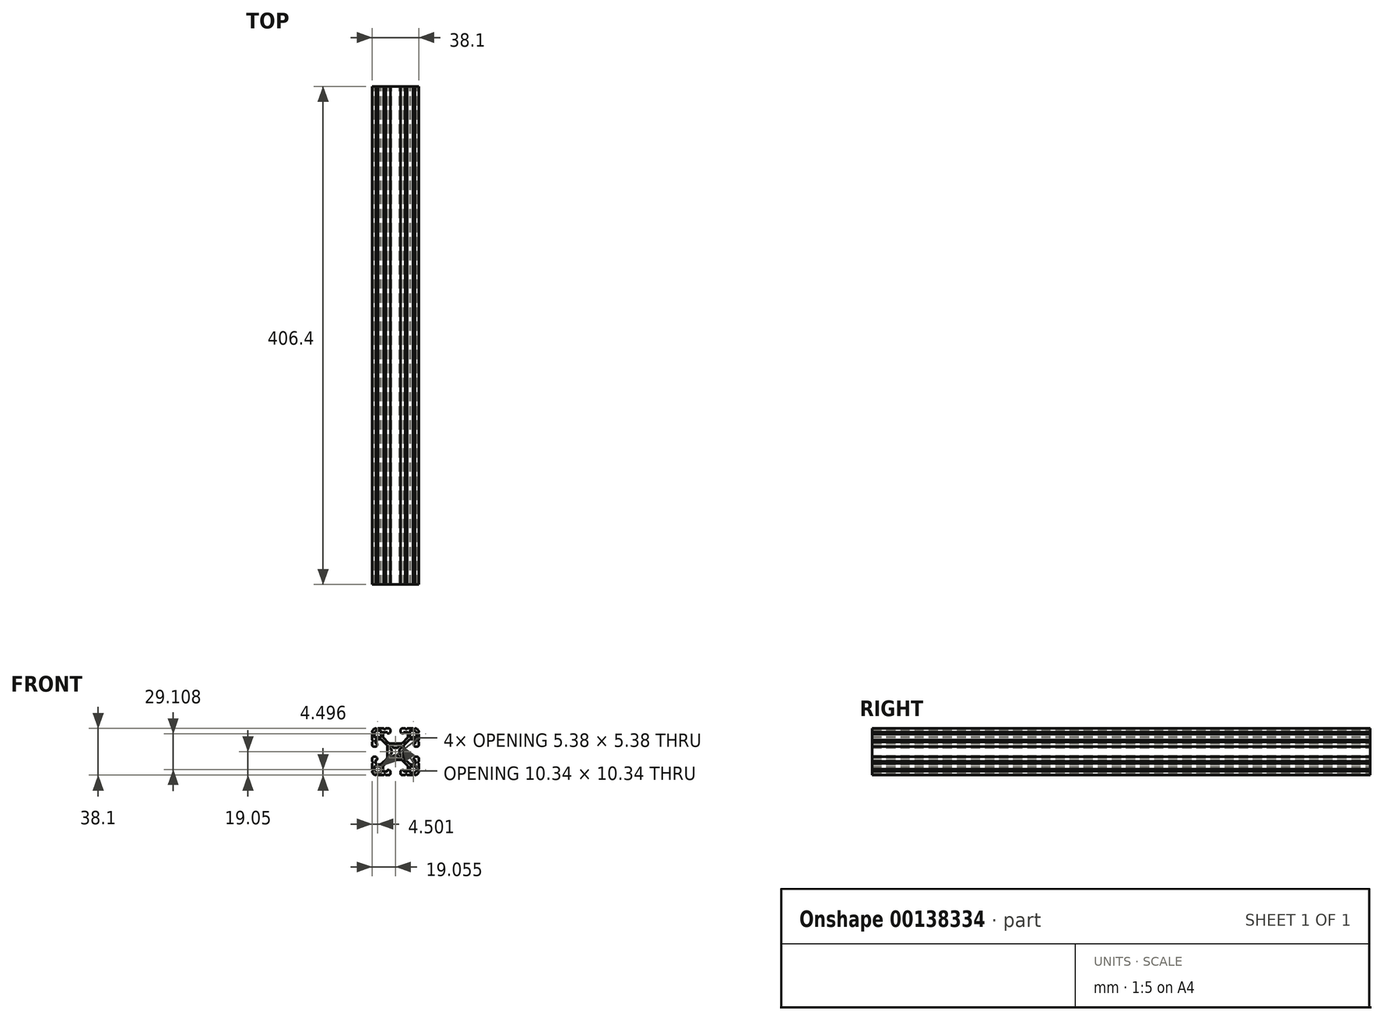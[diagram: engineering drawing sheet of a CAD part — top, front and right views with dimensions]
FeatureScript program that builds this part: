
annotation { "Feature Type Name" : "Feature", "Feature Type Description" : "" }
export const myFeature = defineFeature(function(context is Context, id is Id, definition is map)
    precondition{}
    {
        {
            var Q0;
            Q0=qCreatedBy(makeId("Front.planeOp"),FACE);
            var sketch = newSketch(context, id + "F0", { "sketchPlane" : qUnion([Q0])});
            skLineSegment(sketch, "E0", {"start": v(-126.4, 59.55) * mm, "end": v(-126.4, 54.72) * mm});
            skArc(sketch, "E1", {"start": v(-126.4, 53.2) * mm, "mid": v(-125.63, 53.96) * mm, "end": v(-126.4, 54.72) * mm});
            skArc(sketch, "E2", {"start": v(-126.4, 53.2) * mm, "mid": v(-125.47, 50.93) * mm, "end": v(-123.2, 50) * mm});
            skArc(sketch, "E3", {"start": v(-121.67, 50) * mm, "mid": v(-122.43, 50.76) * mm, "end": v(-123.2, 50) * mm});
            skLineSegment(sketch, "E4", {"start": v(-121.67, 50) * mm, "end": v(-116.84, 50) * mm});
            skArc(sketch, "E5", {"start": v(-115.32, 50) * mm, "mid": v(-116.08, 50.76) * mm, "end": v(-116.84, 50) * mm});
            skLineSegment(sketch, "E6", {"start": v(-115.32, 50) * mm, "end": v(-112.98, 50) * mm});
            skArc(sketch, "E7", {"start": v(-112.98, 50) * mm, "mid": v(-111.87, 50.46) * mm, "end": v(-111.4, 51.57) * mm});
            skLineSegment(sketch, "E8", {"start": v(-111.4, 51.57) * mm, "end": v(-111.4, 52.49) * mm});
            skArc(sketch, "E9", {"start": v(-111.4, 52.49) * mm, "mid": v(-111.87, 53.6) * mm, "end": v(-112.98, 54.06) * mm});
            skLineSegment(sketch, "E10", {"start": v(-112.98, 54.06) * mm, "end": v(-113.7, 54.06) * mm});
            skArc(sketch, "E11", {"start": v(-113.7, 54.06) * mm, "mid": v(-113.96, 53.95) * mm, "end": v(-114.08, 53.68) * mm});
            skLineSegment(sketch, "E12", {"start": v(-114.08, 53.68) * mm, "end": v(-114.08, 53.35) * mm});
            skArc(sketch, "E13", {"start": v(-114.46, 52.97) * mm, "mid": v(-114.19, 53.08) * mm, "end": v(-114.08, 53.35) * mm});
            skLineSegment(sketch, "E14", {"start": v(-114.46, 52.97) * mm, "end": v(-116.74, 52.97) * mm});
            skArc(sketch, "E15", {"start": v(-117.63, 53.86) * mm, "mid": v(-117.37, 53.23) * mm, "end": v(-116.74, 52.97) * mm});
            skLineSegment(sketch, "E16", {"start": v(-117.63, 53.86) * mm, "end": v(-117.63, 56.67) * mm});
            skArc(sketch, "E17", {"start": v(-117.26, 57.57) * mm, "mid": v(-117.54, 57.16) * mm, "end": v(-117.63, 56.67) * mm});
            skLineSegment(sketch, "E18", {"start": v(-117.26, 57.57) * mm, "end": v(-112.9, 61.93) * mm});
            skArc(sketch, "E19", {"start": v(-112, 62.3) * mm, "mid": v(-112.49, 62.2) * mm, "end": v(-112.9, 61.93) * mm});
            skLineSegment(sketch, "E20", {"start": v(-112, 62.3) * mm, "end": v(-102.7, 62.3) * mm});
            skArc(sketch, "E21", {"start": v(-101.8, 61.93) * mm, "mid": v(-102.2, 62.2) * mm, "end": v(-102.7, 62.3) * mm});
            skLineSegment(sketch, "E22", {"start": v(-101.8, 61.93) * mm, "end": v(-97.43, 57.57) * mm});
            skArc(sketch, "E23", {"start": v(-97.06, 56.67) * mm, "mid": v(-97.15, 57.16) * mm, "end": v(-97.43, 57.57) * mm});
            skLineSegment(sketch, "E24", {"start": v(-97.06, 56.67) * mm, "end": v(-97.06, 53.86) * mm});
            skArc(sketch, "E25", {"start": v(-97.95, 52.97) * mm, "mid": v(-97.32, 53.23) * mm, "end": v(-97.06, 53.86) * mm});
            skLineSegment(sketch, "E26", {"start": v(-97.95, 52.97) * mm, "end": v(-100.23, 52.97) * mm});
            skArc(sketch, "E27", {"start": v(-100.61, 53.35) * mm, "mid": v(-100.5, 53.08) * mm, "end": v(-100.23, 52.97) * mm});
            skLineSegment(sketch, "E28", {"start": v(-100.61, 53.35) * mm, "end": v(-100.61, 53.68) * mm});
            skArc(sketch, "E29", {"start": v(-100.61, 53.68) * mm, "mid": v(-100.73, 53.95) * mm, "end": v(-101, 54.06) * mm});
            skLineSegment(sketch, "E30", {"start": v(-101, 54.06) * mm, "end": v(-101.7, 54.06) * mm});
            skArc(sketch, "E31", {"start": v(-101.7, 54.06) * mm, "mid": v(-102.82, 53.6) * mm, "end": v(-103.28, 52.49) * mm});
            skLineSegment(sketch, "E32", {"start": v(-103.28, 52.49) * mm, "end": v(-103.28, 51.57) * mm});
            skArc(sketch, "E33", {"start": v(-103.28, 51.57) * mm, "mid": v(-102.82, 50.46) * mm, "end": v(-101.7, 50) * mm});
            skLineSegment(sketch, "E34", {"start": v(-101.7, 50) * mm, "end": v(-99.37, 50) * mm});
            skArc(sketch, "E35", {"start": v(-97.85, 50) * mm, "mid": v(-98.6, 50.76) * mm, "end": v(-99.37, 50) * mm});
            skLineSegment(sketch, "E36", {"start": v(-97.85, 50) * mm, "end": v(-93.02, 50) * mm});
            skArc(sketch, "E37", {"start": v(-91.5, 50) * mm, "mid": v(-92.26, 50.76) * mm, "end": v(-93.02, 50) * mm});
            skArc(sketch, "E38", {"start": v(-91.5, 50) * mm, "mid": v(-89.23, 50.93) * mm, "end": v(-88.3, 53.2) * mm});
            skArc(sketch, "E39", {"start": v(-88.3, 54.72) * mm, "mid": v(-89.06, 53.96) * mm, "end": v(-88.3, 53.2) * mm});
            skLineSegment(sketch, "E40", {"start": v(-88.3, 54.72) * mm, "end": v(-88.3, 59.55) * mm});
            skArc(sketch, "E41", {"start": v(-88.3, 61.07) * mm, "mid": v(-89.06, 60.31) * mm, "end": v(-88.3, 59.55) * mm});
            skLineSegment(sketch, "E42", {"start": v(-88.3, 61.07) * mm, "end": v(-88.3, 63.41) * mm});
            skArc(sketch, "E43", {"start": v(-88.3, 63.41) * mm, "mid": v(-88.76, 64.52) * mm, "end": v(-89.87, 64.99) * mm});
            skLineSegment(sketch, "E44", {"start": v(-89.87, 64.99) * mm, "end": v(-90.78, 64.99) * mm});
            skArc(sketch, "E45", {"start": v(-90.78, 64.99) * mm, "mid": v(-91.9, 64.52) * mm, "end": v(-92.36, 63.41) * mm});
            skLineSegment(sketch, "E46", {"start": v(-92.36, 63.41) * mm, "end": v(-92.36, 62.7) * mm});
            skArc(sketch, "E47", {"start": v(-92.36, 62.7) * mm, "mid": v(-92.25, 62.43) * mm, "end": v(-91.98, 62.32) * mm});
            skLineSegment(sketch, "E48", {"start": v(-91.98, 62.32) * mm, "end": v(-91.65, 62.32) * mm});
            skArc(sketch, "E49", {"start": v(-91.27, 61.94) * mm, "mid": v(-91.38, 62.2) * mm, "end": v(-91.65, 62.32) * mm});
            skLineSegment(sketch, "E50", {"start": v(-91.27, 61.94) * mm, "end": v(-91.27, 59.65) * mm});
            skArc(sketch, "E51", {"start": v(-92.16, 58.76) * mm, "mid": v(-91.53, 59.02) * mm, "end": v(-91.27, 59.65) * mm});
            skLineSegment(sketch, "E52", {"start": v(-92.16, 58.76) * mm, "end": v(-94.97, 58.76) * mm});
            skArc(sketch, "E53", {"start": v(-95.87, 59.13) * mm, "mid": v(-95.46, 58.86) * mm, "end": v(-94.97, 58.76) * mm});
            skLineSegment(sketch, "E54", {"start": v(-95.87, 59.13) * mm, "end": v(-100.23, 63.5) * mm});
            skArc(sketch, "E55", {"start": v(-100.6, 64.4) * mm, "mid": v(-100.5, 63.9) * mm, "end": v(-100.23, 63.5) * mm});
            skLineSegment(sketch, "E56", {"start": v(-100.6, 64.4) * mm, "end": v(-100.6, 73.7) * mm});
            skArc(sketch, "E57", {"start": v(-100.23, 74.6) * mm, "mid": v(-100.5, 74.2) * mm, "end": v(-100.6, 73.7) * mm});
            skLineSegment(sketch, "E58", {"start": v(-100.23, 74.6) * mm, "end": v(-95.87, 78.96) * mm});
            skArc(sketch, "E59", {"start": v(-94.97, 79.34) * mm, "mid": v(-95.46, 79.24) * mm, "end": v(-95.87, 78.96) * mm});
            skLineSegment(sketch, "E60", {"start": v(-94.97, 79.34) * mm, "end": v(-92.16, 79.34) * mm});
            skArc(sketch, "E61", {"start": v(-91.27, 78.45) * mm, "mid": v(-91.53, 79.08) * mm, "end": v(-92.16, 79.34) * mm});
            skLineSegment(sketch, "E62", {"start": v(-91.27, 78.45) * mm, "end": v(-91.27, 76.16) * mm});
            skArc(sketch, "E63", {"start": v(-91.65, 75.78) * mm, "mid": v(-91.38, 75.9) * mm, "end": v(-91.27, 76.16) * mm});
            skLineSegment(sketch, "E64", {"start": v(-91.65, 75.78) * mm, "end": v(-91.98, 75.78) * mm});
            skArc(sketch, "E65", {"start": v(-91.98, 75.78) * mm, "mid": v(-92.25, 75.67) * mm, "end": v(-92.36, 75.4) * mm});
            skLineSegment(sketch, "E66", {"start": v(-92.36, 75.4) * mm, "end": v(-92.36, 74.69) * mm});
            skArc(sketch, "E67", {"start": v(-92.36, 74.69) * mm, "mid": v(-91.9, 73.58) * mm, "end": v(-90.78, 73.11) * mm});
            skLineSegment(sketch, "E68", {"start": v(-90.78, 73.11) * mm, "end": v(-89.87, 73.11) * mm});
            skArc(sketch, "E69", {"start": v(-89.87, 73.11) * mm, "mid": v(-88.76, 73.58) * mm, "end": v(-88.3, 74.69) * mm});
            skLineSegment(sketch, "E70", {"start": v(-88.3, 74.69) * mm, "end": v(-88.3, 77.03) * mm});
            skArc(sketch, "E71", {"start": v(-88.3, 78.55) * mm, "mid": v(-89.06, 77.79) * mm, "end": v(-88.3, 77.03) * mm});
            skLineSegment(sketch, "E72", {"start": v(-88.3, 78.55) * mm, "end": v(-88.3, 83.38) * mm});
            skArc(sketch, "E73", {"start": v(-88.3, 84.9) * mm, "mid": v(-89.06, 84.14) * mm, "end": v(-88.3, 83.38) * mm});
            skArc(sketch, "E74", {"start": v(-88.3, 84.9) * mm, "mid": v(-89.23, 87.17) * mm, "end": v(-91.5, 88.1) * mm});
            skArc(sketch, "E75", {"start": v(-93.02, 88.1) * mm, "mid": v(-92.26, 87.34) * mm, "end": v(-91.5, 88.1) * mm});
            skLineSegment(sketch, "E76", {"start": v(-93.02, 88.1) * mm, "end": v(-97.85, 88.1) * mm});
            skArc(sketch, "E77", {"start": v(-99.37, 88.1) * mm, "mid": v(-98.6, 87.34) * mm, "end": v(-97.85, 88.1) * mm});
            skLineSegment(sketch, "E78", {"start": v(-99.37, 88.1) * mm, "end": v(-101.7, 88.1) * mm});
            skArc(sketch, "E79", {"start": v(-101.7, 88.1) * mm, "mid": v(-102.82, 87.64) * mm, "end": v(-103.28, 86.53) * mm});
            skLineSegment(sketch, "E80", {"start": v(-103.28, 86.53) * mm, "end": v(-103.28, 85.61) * mm});
            skArc(sketch, "E81", {"start": v(-103.28, 85.61) * mm, "mid": v(-102.82, 84.5) * mm, "end": v(-101.7, 84.04) * mm});
            skLineSegment(sketch, "E82", {"start": v(-101.7, 84.04) * mm, "end": v(-101, 84.04) * mm});
            skArc(sketch, "E83", {"start": v(-101, 84.04) * mm, "mid": v(-100.73, 84.15) * mm, "end": v(-100.61, 84.42) * mm});
            skLineSegment(sketch, "E84", {"start": v(-100.61, 84.42) * mm, "end": v(-100.61, 84.75) * mm});
            skArc(sketch, "E85", {"start": v(-100.23, 85.13) * mm, "mid": v(-100.5, 85.02) * mm, "end": v(-100.61, 84.75) * mm});
            skLineSegment(sketch, "E86", {"start": v(-100.23, 85.13) * mm, "end": v(-97.95, 85.13) * mm});
            skArc(sketch, "E87", {"start": v(-97.06, 84.24) * mm, "mid": v(-97.32, 84.87) * mm, "end": v(-97.95, 85.13) * mm});
            skLineSegment(sketch, "E88", {"start": v(-97.06, 84.24) * mm, "end": v(-97.06, 81.43) * mm});
            skArc(sketch, "E89", {"start": v(-97.43, 80.53) * mm, "mid": v(-97.15, 80.94) * mm, "end": v(-97.06, 81.43) * mm});
            skLineSegment(sketch, "E90", {"start": v(-97.43, 80.53) * mm, "end": v(-101.8, 76.17) * mm});
            skArc(sketch, "E91", {"start": v(-102.7, 75.8) * mm, "mid": v(-102.2, 75.9) * mm, "end": v(-101.8, 76.17) * mm});
            skLineSegment(sketch, "E92", {"start": v(-102.7, 75.8) * mm, "end": v(-112, 75.8) * mm});
            skArc(sketch, "E93", {"start": v(-112.9, 76.17) * mm, "mid": v(-112.49, 75.9) * mm, "end": v(-112, 75.8) * mm});
            skLineSegment(sketch, "E94", {"start": v(-112.9, 76.17) * mm, "end": v(-117.26, 80.53) * mm});
            skArc(sketch, "E95", {"start": v(-117.63, 81.43) * mm, "mid": v(-117.54, 80.94) * mm, "end": v(-117.26, 80.53) * mm});
            skLineSegment(sketch, "E96", {"start": v(-117.63, 81.43) * mm, "end": v(-117.63, 84.24) * mm});
            skArc(sketch, "E97", {"start": v(-116.74, 85.13) * mm, "mid": v(-117.37, 84.87) * mm, "end": v(-117.63, 84.24) * mm});
            skLineSegment(sketch, "E98", {"start": v(-116.74, 85.13) * mm, "end": v(-114.46, 85.13) * mm});
            skArc(sketch, "E99", {"start": v(-114.08, 84.75) * mm, "mid": v(-114.19, 85.02) * mm, "end": v(-114.46, 85.13) * mm});
            skLineSegment(sketch, "E100", {"start": v(-114.08, 84.75) * mm, "end": v(-114.08, 84.42) * mm});
            skArc(sketch, "E101", {"start": v(-114.08, 84.42) * mm, "mid": v(-113.96, 84.15) * mm, "end": v(-113.7, 84.04) * mm});
            skLineSegment(sketch, "E102", {"start": v(-113.7, 84.04) * mm, "end": v(-112.98, 84.04) * mm});
            skArc(sketch, "E103", {"start": v(-112.98, 84.04) * mm, "mid": v(-111.87, 84.5) * mm, "end": v(-111.4, 85.61) * mm});
            skLineSegment(sketch, "E104", {"start": v(-111.4, 85.61) * mm, "end": v(-111.4, 86.53) * mm});
            skArc(sketch, "E105", {"start": v(-111.4, 86.53) * mm, "mid": v(-111.87, 87.64) * mm, "end": v(-112.98, 88.1) * mm});
            skLineSegment(sketch, "E106", {"start": v(-112.98, 88.1) * mm, "end": v(-115.32, 88.1) * mm});
            skArc(sketch, "E107", {"start": v(-116.84, 88.1) * mm, "mid": v(-116.08, 87.34) * mm, "end": v(-115.32, 88.1) * mm});
            skLineSegment(sketch, "E108", {"start": v(-116.84, 88.1) * mm, "end": v(-121.67, 88.1) * mm});
            skArc(sketch, "E109", {"start": v(-123.2, 88.1) * mm, "mid": v(-122.43, 87.34) * mm, "end": v(-121.67, 88.1) * mm});
            skArc(sketch, "E110", {"start": v(-123.2, 88.1) * mm, "mid": v(-125.47, 87.17) * mm, "end": v(-126.4, 84.9) * mm});
            skArc(sketch, "E111", {"start": v(-126.4, 83.38) * mm, "mid": v(-125.63, 84.14) * mm, "end": v(-126.4, 84.9) * mm});
            skLineSegment(sketch, "E112", {"start": v(-126.4, 83.38) * mm, "end": v(-126.4, 78.55) * mm});
            skArc(sketch, "E113", {"start": v(-126.4, 77.03) * mm, "mid": v(-125.63, 77.79) * mm, "end": v(-126.4, 78.55) * mm});
            skLineSegment(sketch, "E114", {"start": v(-126.4, 77.03) * mm, "end": v(-126.4, 74.69) * mm});
            skArc(sketch, "E115", {"start": v(-126.4, 74.69) * mm, "mid": v(-125.93, 73.58) * mm, "end": v(-124.82, 73.11) * mm});
            skLineSegment(sketch, "E116", {"start": v(-124.82, 73.11) * mm, "end": v(-123.9, 73.11) * mm});
            skArc(sketch, "E117", {"start": v(-123.9, 73.11) * mm, "mid": v(-122.8, 73.58) * mm, "end": v(-122.33, 74.69) * mm});
            skLineSegment(sketch, "E118", {"start": v(-122.33, 74.69) * mm, "end": v(-122.33, 75.4) * mm});
            skArc(sketch, "E119", {"start": v(-122.33, 75.4) * mm, "mid": v(-122.44, 75.67) * mm, "end": v(-122.71, 75.78) * mm});
            skLineSegment(sketch, "E120", {"start": v(-122.71, 75.78) * mm, "end": v(-123.04, 75.78) * mm});
            skArc(sketch, "E121", {"start": v(-123.42, 76.16) * mm, "mid": v(-123.31, 75.9) * mm, "end": v(-123.04, 75.78) * mm});
            skLineSegment(sketch, "E122", {"start": v(-123.42, 76.16) * mm, "end": v(-123.42, 78.45) * mm});
            skArc(sketch, "E123", {"start": v(-122.53, 79.34) * mm, "mid": v(-123.16, 79.08) * mm, "end": v(-123.42, 78.45) * mm});
            skLineSegment(sketch, "E124", {"start": v(-122.53, 79.34) * mm, "end": v(-119.72, 79.34) * mm});
            skArc(sketch, "E125", {"start": v(-118.82, 78.96) * mm, "mid": v(-119.23, 79.24) * mm, "end": v(-119.72, 79.34) * mm});
            skLineSegment(sketch, "E126", {"start": v(-118.82, 78.96) * mm, "end": v(-114.46, 74.6) * mm});
            skArc(sketch, "E127", {"start": v(-114.09, 73.7) * mm, "mid": v(-114.19, 74.2) * mm, "end": v(-114.46, 74.6) * mm});
            skLineSegment(sketch, "E128", {"start": v(-114.09, 73.7) * mm, "end": v(-114.09, 64.4) * mm});
            skArc(sketch, "E129", {"start": v(-114.46, 63.5) * mm, "mid": v(-114.19, 63.9) * mm, "end": v(-114.09, 64.4) * mm});
            skLineSegment(sketch, "E130", {"start": v(-114.46, 63.5) * mm, "end": v(-118.82, 59.13) * mm});
            skArc(sketch, "E131", {"start": v(-119.72, 58.76) * mm, "mid": v(-119.23, 58.86) * mm, "end": v(-118.82, 59.13) * mm});
            skLineSegment(sketch, "E132", {"start": v(-119.72, 58.76) * mm, "end": v(-122.53, 58.76) * mm});
            skArc(sketch, "E133", {"start": v(-123.42, 59.65) * mm, "mid": v(-123.16, 59.02) * mm, "end": v(-122.53, 58.76) * mm});
            skLineSegment(sketch, "E134", {"start": v(-123.42, 59.65) * mm, "end": v(-123.42, 61.94) * mm});
            skArc(sketch, "E135", {"start": v(-123.04, 62.32) * mm, "mid": v(-123.31, 62.2) * mm, "end": v(-123.42, 61.94) * mm});
            skLineSegment(sketch, "E136", {"start": v(-123.04, 62.32) * mm, "end": v(-122.71, 62.32) * mm});
            skArc(sketch, "E137", {"start": v(-122.71, 62.32) * mm, "mid": v(-122.44, 62.43) * mm, "end": v(-122.33, 62.7) * mm});
            skLineSegment(sketch, "E138", {"start": v(-122.33, 62.7) * mm, "end": v(-122.33, 63.41) * mm});
            skArc(sketch, "E139", {"start": v(-122.33, 63.41) * mm, "mid": v(-122.8, 64.52) * mm, "end": v(-123.9, 64.99) * mm});
            skLineSegment(sketch, "E140", {"start": v(-123.9, 64.99) * mm, "end": v(-124.82, 64.99) * mm});
            skArc(sketch, "E141", {"start": v(-124.82, 64.99) * mm, "mid": v(-125.93, 64.52) * mm, "end": v(-126.4, 63.41) * mm});
            skLineSegment(sketch, "E142", {"start": v(-126.4, 63.41) * mm, "end": v(-126.4, 61.07) * mm});
            skArc(sketch, "E143", {"start": v(-95.1, 86.3) * mm, "mid": v(-95.37, 86.18) * mm, "end": v(-95.48, 85.92) * mm});
            skLineSegment(sketch, "E144", {"start": v(-92.9, 86.3) * mm, "end": v(-95.1, 86.3) * mm});
            skArc(sketch, "E145", {"start": v(-90.1, 83.5) * mm, "mid": v(-90.92, 85.48) * mm, "end": v(-92.9, 86.3) * mm});
            skLineSegment(sketch, "E146", {"start": v(-90.1, 81.3) * mm, "end": v(-90.1, 83.5) * mm});
            skArc(sketch, "E147", {"start": v(-90.48, 80.91) * mm, "mid": v(-90.21, 81.02) * mm, "end": v(-90.1, 81.3) * mm});
            skLineSegment(sketch, "E148", {"start": v(-92.25, 80.91) * mm, "end": v(-90.48, 80.91) * mm});
            skLineSegment(sketch, "E149", {"start": v(-92.8, 81.45) * mm, "end": v(-92.25, 80.91) * mm});
            skLineSegment(sketch, "E150", {"start": v(-93.33, 80.91) * mm, "end": v(-92.8, 81.45) * mm});
            skLineSegment(sketch, "E151", {"start": v(-95.1, 80.91) * mm, "end": v(-93.33, 80.91) * mm});
            skArc(sketch, "E152", {"start": v(-95.48, 81.3) * mm, "mid": v(-95.37, 81.02) * mm, "end": v(-95.1, 80.91) * mm});
            skLineSegment(sketch, "E153", {"start": v(-95.48, 83.07) * mm, "end": v(-95.48, 81.3) * mm});
            skLineSegment(sketch, "E154", {"start": v(-94.94, 83.6) * mm, "end": v(-95.48, 83.07) * mm});
            skLineSegment(sketch, "E155", {"start": v(-95.48, 84.14) * mm, "end": v(-94.94, 83.6) * mm});
            skLineSegment(sketch, "E156", {"start": v(-95.48, 56.8) * mm, "end": v(-95.48, 55.03) * mm});
            skArc(sketch, "E157", {"start": v(-95.1, 57.19) * mm, "mid": v(-95.37, 57.08) * mm, "end": v(-95.48, 56.8) * mm});
            skLineSegment(sketch, "E158", {"start": v(-93.33, 57.19) * mm, "end": v(-95.1, 57.19) * mm});
            skLineSegment(sketch, "E159", {"start": v(-92.8, 56.65) * mm, "end": v(-93.33, 57.19) * mm});
            skLineSegment(sketch, "E160", {"start": v(-92.25, 57.19) * mm, "end": v(-92.8, 56.65) * mm});
            skLineSegment(sketch, "E161", {"start": v(-90.48, 57.19) * mm, "end": v(-92.25, 57.19) * mm});
            skArc(sketch, "E162", {"start": v(-90.1, 56.8) * mm, "mid": v(-90.21, 57.08) * mm, "end": v(-90.48, 57.19) * mm});
            skLineSegment(sketch, "E163", {"start": v(-90.1, 54.6) * mm, "end": v(-90.1, 56.8) * mm});
            skArc(sketch, "E164", {"start": v(-92.9, 51.8) * mm, "mid": v(-90.92, 52.62) * mm, "end": v(-90.1, 54.6) * mm});
            skLineSegment(sketch, "E165", {"start": v(-95.1, 51.8) * mm, "end": v(-92.9, 51.8) * mm});
            skArc(sketch, "E166", {"start": v(-95.48, 52.18) * mm, "mid": v(-95.37, 51.91) * mm, "end": v(-95.1, 51.8) * mm});
            skLineSegment(sketch, "E167", {"start": v(-95.48, 53.96) * mm, "end": v(-95.48, 52.18) * mm});
            skLineSegment(sketch, "E168", {"start": v(-94.94, 54.5) * mm, "end": v(-95.48, 53.96) * mm});
            skLineSegment(sketch, "E169", {"start": v(-112.51, 65.13) * mm, "end": v(-112.51, 64.14) * mm});
            skArc(sketch, "E170", {"start": v(-112.25, 65.76) * mm, "mid": v(-112.45, 65.47) * mm, "end": v(-112.51, 65.13) * mm});
            skLineSegment(sketch, "E171", {"start": v(-110.54, 67.47) * mm, "end": v(-112.25, 65.76) * mm});
            skArc(sketch, "E172", {"start": v(-110.54, 67.47) * mm, "mid": v(-110.44, 67.66) * mm, "end": v(-110.46, 67.87) * mm});
            skArc(sketch, "E173", {"start": v(-110.46, 70.23) * mm, "mid": v(-110.67, 69.05) * mm, "end": v(-110.46, 67.87) * mm});
            skArc(sketch, "E174", {"start": v(-110.46, 70.23) * mm, "mid": v(-110.44, 70.44) * mm, "end": v(-110.54, 70.63) * mm});
            skLineSegment(sketch, "E175", {"start": v(-112.25, 72.34) * mm, "end": v(-110.54, 70.63) * mm});
            skArc(sketch, "E176", {"start": v(-112.51, 72.97) * mm, "mid": v(-112.45, 72.63) * mm, "end": v(-112.25, 72.34) * mm});
            skLineSegment(sketch, "E177", {"start": v(-112.51, 73.96) * mm, "end": v(-112.51, 72.97) * mm});
            skArc(sketch, "E178", {"start": v(-112.26, 74.22) * mm, "mid": v(-112.44, 74.14) * mm, "end": v(-112.51, 73.96) * mm});
            skLineSegment(sketch, "E179", {"start": v(-111.27, 74.22) * mm, "end": v(-112.26, 74.22) * mm});
            skArc(sketch, "E180", {"start": v(-110.64, 73.96) * mm, "mid": v(-110.93, 74.15) * mm, "end": v(-111.27, 74.22) * mm});
            skLineSegment(sketch, "E181", {"start": v(-108.93, 72.25) * mm, "end": v(-110.64, 73.96) * mm});
            skArc(sketch, "E182", {"start": v(-108.93, 72.25) * mm, "mid": v(-108.74, 72.15) * mm, "end": v(-108.52, 72.16) * mm});
            skArc(sketch, "E183", {"start": v(-106.17, 72.16) * mm, "mid": v(-107.35, 72.38) * mm, "end": v(-108.52, 72.16) * mm});
            skArc(sketch, "E184", {"start": v(-106.17, 72.16) * mm, "mid": v(-105.95, 72.15) * mm, "end": v(-105.76, 72.25) * mm});
            skLineSegment(sketch, "E185", {"start": v(-104.05, 73.96) * mm, "end": v(-105.76, 72.25) * mm});
            skArc(sketch, "E186", {"start": v(-103.42, 74.22) * mm, "mid": v(-103.76, 74.15) * mm, "end": v(-104.05, 73.96) * mm});
            skLineSegment(sketch, "E187", {"start": v(-102.43, 74.22) * mm, "end": v(-103.42, 74.22) * mm});
            skArc(sketch, "E188", {"start": v(-102.18, 73.96) * mm, "mid": v(-102.25, 74.14) * mm, "end": v(-102.43, 74.22) * mm});
            skLineSegment(sketch, "E189", {"start": v(-102.18, 72.97) * mm, "end": v(-102.18, 73.96) * mm});
            skArc(sketch, "E190", {"start": v(-102.44, 72.34) * mm, "mid": v(-102.24, 72.63) * mm, "end": v(-102.18, 72.97) * mm});
            skLineSegment(sketch, "E191", {"start": v(-104.15, 70.63) * mm, "end": v(-102.44, 72.34) * mm});
            skArc(sketch, "E192", {"start": v(-104.15, 70.63) * mm, "mid": v(-104.25, 70.44) * mm, "end": v(-104.23, 70.23) * mm});
            skArc(sketch, "E193", {"start": v(-104.23, 67.87) * mm, "mid": v(-104.02, 69.05) * mm, "end": v(-104.23, 70.23) * mm});
            skArc(sketch, "E194", {"start": v(-104.23, 67.87) * mm, "mid": v(-104.25, 67.66) * mm, "end": v(-104.15, 67.47) * mm});
            skLineSegment(sketch, "E195", {"start": v(-102.44, 65.76) * mm, "end": v(-104.15, 67.47) * mm});
            skArc(sketch, "E196", {"start": v(-102.18, 65.13) * mm, "mid": v(-102.24, 65.47) * mm, "end": v(-102.44, 65.76) * mm});
            skLineSegment(sketch, "E197", {"start": v(-102.18, 64.14) * mm, "end": v(-102.18, 65.13) * mm});
            skArc(sketch, "E198", {"start": v(-102.43, 63.88) * mm, "mid": v(-102.25, 63.96) * mm, "end": v(-102.18, 64.14) * mm});
            skLineSegment(sketch, "E199", {"start": v(-103.42, 63.88) * mm, "end": v(-102.43, 63.88) * mm});
            skArc(sketch, "E200", {"start": v(-104.05, 64.14) * mm, "mid": v(-103.76, 63.95) * mm, "end": v(-103.42, 63.88) * mm});
            skLineSegment(sketch, "E201", {"start": v(-105.76, 65.85) * mm, "end": v(-104.05, 64.14) * mm});
            skArc(sketch, "E202", {"start": v(-105.76, 65.85) * mm, "mid": v(-105.95, 65.95) * mm, "end": v(-106.17, 65.94) * mm});
            skArc(sketch, "E203", {"start": v(-108.52, 65.94) * mm, "mid": v(-107.35, 65.72) * mm, "end": v(-106.17, 65.94) * mm});
            skArc(sketch, "E204", {"start": v(-108.52, 65.94) * mm, "mid": v(-108.74, 65.95) * mm, "end": v(-108.93, 65.85) * mm});
            skLineSegment(sketch, "E205", {"start": v(-110.64, 64.14) * mm, "end": v(-108.93, 65.85) * mm});
            skArc(sketch, "E206", {"start": v(-111.27, 63.88) * mm, "mid": v(-110.93, 63.95) * mm, "end": v(-110.64, 64.14) * mm});
            skLineSegment(sketch, "E207", {"start": v(-112.26, 63.88) * mm, "end": v(-111.27, 63.88) * mm});
            skLineSegment(sketch, "E208", {"start": v(-124.6, 56.8) * mm, "end": v(-124.6, 54.6) * mm});
            skArc(sketch, "E209", {"start": v(-124.21, 57.19) * mm, "mid": v(-124.48, 57.08) * mm, "end": v(-124.6, 56.8) * mm});
            skLineSegment(sketch, "E210", {"start": v(-122.44, 57.19) * mm, "end": v(-124.21, 57.19) * mm});
            skLineSegment(sketch, "E211", {"start": v(-121.9, 56.65) * mm, "end": v(-122.44, 57.19) * mm});
            skLineSegment(sketch, "E212", {"start": v(-121.36, 57.19) * mm, "end": v(-121.9, 56.65) * mm});
            skLineSegment(sketch, "E213", {"start": v(-119.59, 57.19) * mm, "end": v(-121.36, 57.19) * mm});
            skArc(sketch, "E214", {"start": v(-119.2, 56.8) * mm, "mid": v(-119.32, 57.08) * mm, "end": v(-119.59, 57.19) * mm});
            skLineSegment(sketch, "E215", {"start": v(-119.2, 55.03) * mm, "end": v(-119.2, 56.8) * mm});
            skLineSegment(sketch, "E216", {"start": v(-119.75, 54.5) * mm, "end": v(-119.2, 55.03) * mm});
            skLineSegment(sketch, "E217", {"start": v(-119.2, 53.96) * mm, "end": v(-119.75, 54.5) * mm});
            skLineSegment(sketch, "E218", {"start": v(-119.2, 52.18) * mm, "end": v(-119.2, 53.96) * mm});
            skArc(sketch, "E219", {"start": v(-119.59, 51.8) * mm, "mid": v(-119.32, 51.91) * mm, "end": v(-119.2, 52.18) * mm});
            skLineSegment(sketch, "E220", {"start": v(-121.8, 51.8) * mm, "end": v(-119.59, 51.8) * mm});
            skLineSegment(sketch, "E221", {"start": v(-124.6, 83.5) * mm, "end": v(-124.6, 81.3) * mm});
            skArc(sketch, "E222", {"start": v(-121.8, 86.3) * mm, "mid": v(-123.77, 85.48) * mm, "end": v(-124.6, 83.5) * mm});
            skLineSegment(sketch, "E223", {"start": v(-119.59, 86.3) * mm, "end": v(-121.8, 86.3) * mm});
            skArc(sketch, "E224", {"start": v(-119.2, 85.92) * mm, "mid": v(-119.32, 86.18) * mm, "end": v(-119.59, 86.3) * mm});
            skLineSegment(sketch, "E225", {"start": v(-119.2, 84.14) * mm, "end": v(-119.2, 85.92) * mm});
            skLineSegment(sketch, "E226", {"start": v(-119.75, 83.6) * mm, "end": v(-119.2, 84.14) * mm});
            skLineSegment(sketch, "E227", {"start": v(-119.2, 83.07) * mm, "end": v(-119.75, 83.6) * mm});
            skLineSegment(sketch, "E228", {"start": v(-119.2, 81.3) * mm, "end": v(-119.2, 83.07) * mm});
            skArc(sketch, "E229", {"start": v(-119.59, 80.91) * mm, "mid": v(-119.32, 81.02) * mm, "end": v(-119.2, 81.3) * mm});
            skLineSegment(sketch, "E230", {"start": v(-121.36, 80.91) * mm, "end": v(-119.59, 80.91) * mm});
            skLineSegment(sketch, "E231", {"start": v(-121.9, 81.45) * mm, "end": v(-121.36, 80.91) * mm});
            skLineSegment(sketch, "E232", {"start": v(-122.44, 80.91) * mm, "end": v(-121.9, 81.45) * mm});
            skLineSegment(sketch, "E233", {"start": v(-124.21, 80.91) * mm, "end": v(-122.44, 80.91) * mm});
            skLineSegment(sketch, "E234", {"start": v(-95.48, 85.92) * mm, "end": v(-95.48, 84.14) * mm});
            skLineSegment(sketch, "E235", {"start": v(-95.48, 55.03) * mm, "end": v(-94.94, 54.5) * mm});
            skArc(sketch, "E236", {"start": v(-112.51, 64.14) * mm, "mid": v(-112.44, 63.96) * mm, "end": v(-112.26, 63.88) * mm});
            skArc(sketch, "E237", {"start": v(-124.6, 54.6) * mm, "mid": v(-123.77, 52.62) * mm, "end": v(-121.8, 51.8) * mm});
            skArc(sketch, "E238", {"start": v(-124.6, 81.3) * mm, "mid": v(-124.48, 81.02) * mm, "end": v(-124.21, 80.91) * mm});
            skArc(sketch, "E239", {"start": v(-126.4, 59.55) * mm, "mid": v(-125.63, 60.31) * mm, "end": v(-126.4, 61.07) * mm});
            skSolve(sketch);
        }
        {
            var Q0;
            Q0=makeQuery(id+"F0.imprint","IMPRINT",FACE,{"disambiguationData":[TD([[makeQuery(id+"F0.imprint","IMPRINT",EDGE,{"derivedFrom":sQuery(id+"F0.wireOp",EDGE,"E0")}),1.0]])]});
            extrude(context, id + "F1", {"entities" : qUnion([Q0]), "endBound" : BoundingType.SYMMETRIC, "depth" : 406.4 * mm});
        }
    });
